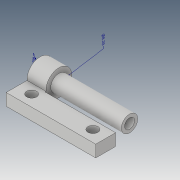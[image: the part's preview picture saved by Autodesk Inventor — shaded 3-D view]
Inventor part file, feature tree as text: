
AUTODESK INVENTOR PART (.ipt)
format: ipt  version: 2019 (Build 230136000, 136)  size: 184,832 bytes
history: native  units: mm
features: extrude x7, other x6, sketch x6, plane x5, move_body x2, fillet x1, direct_edit x1, projected_geometry x1
ambient origin geometry x8: Origin, YZ Plane, XZ Plane, XY Plane, X Axis, Y Axis, Z Axis, Center Point
bodies: Solid1 (feature_tree)
feature tree (29):
  other  "Annotations"
  extrude  "Extrusion1"  Depth=45.0mm
  sketch  "Sketch4"  dims[d5=5.0mm d6=5.0mm d7=11.0mm]
  extrude  "Extrusion4"  Depth=5.0mm
  fillet  "Fillet1"  Radius=11.0mm
  extrude  "Extrusion5"  Depth=23.0mm
  plane  "Work Plane1"
  extrude  "Extrusion6"  Depth=10.0mm
  plane  "Work Plane8"
  plane  "Work Plane10"
  sketch  "Sketch11"  dims[d24=3.0mm d25=0.0mm d26=12.0mm]
  plane  "Work Plane11"
  plane  "Work Plane12"
  extrude  "Extrusion10"  Depth=12.0mm
  extrude  "Extrusion11"  Depth=6.5mm TaperAngle=0.0deg
  direct_edit  "Direct Edit1"
  extrude  "Extrusion13"  Depth=6.5mm
  sketch  "Sketch1"  dims[d0=6.0mm d1=0.0mm d4=45.0mm]
  sketch  "Sketch5"  dims[d8=11.0mm d9=23.0mm]
  sketch  "Sketch6"  dims[d10=10.0mm d20=13.0mm]
  projected_geometry  "Projected Loop4"
  sketch  "Sketch13"  dims[d27=5.0mm d28=3.0mm d29=0.0mm d33=5.0mm d34=5.0mm d35=17.8mm d36=7.0mm d37=17.8mm d38=7.1mm d39=30.8mm d40=7.1mm d41=3.0mm d42=0.0mm d52=0.0mm d53=0.0mm d54=0.0mm d55=10.0mm d56=0.0mm d57=10.0mm d58=0.0mm d59=0.0mm d60=0.0mm d61=-1.5mm d62=0.0mm d63=0.0mm d64=-17.25mm d68=1.6mm d69=10.0mm d70=0.0mm d71=35.626875mm d72=6.5mm d75=48.705644mm d76=8.2mm]
  move_body  "Move1"
  move_body  "Move2"
  other  "Radial Dimension 1"
  other  "Diameter Dimension 1"
  parser-record x1  (decoder bookkeeping rows leaked as tree rows — omitted from the tree; the rows remain in map.json)
  other  "Cerniera Assemb.iam"
  other  "Cerniera 1:2"
note: 1 file-system path scrubbed to <path> (originals preserved in map.json)
